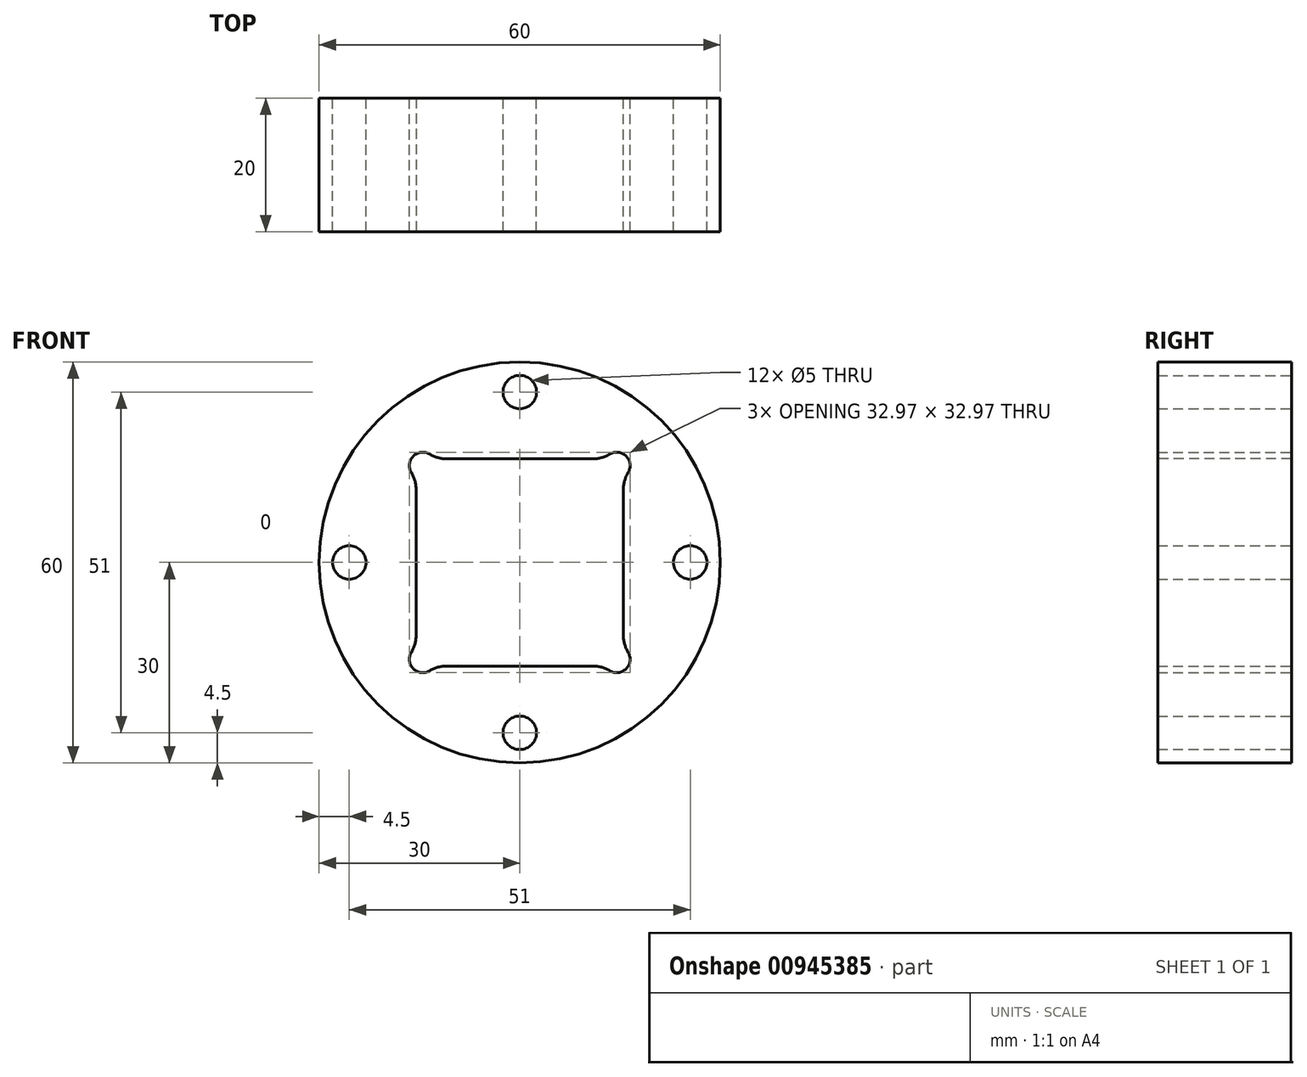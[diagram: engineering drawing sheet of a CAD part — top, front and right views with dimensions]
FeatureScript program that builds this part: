
annotation { "Feature Type Name" : "Feature", "Feature Type Description" : "" }
export const myFeature = defineFeature(function(context is Context, id is Id, definition is map)
    precondition{}
    {
        {
            var Q0;
            Q0=qCreatedBy(makeId("Front.planeOp"),FACE);
            var sketch = newSketch(context, id + "F0", { "sketchPlane" : qUnion([Q0])});
            skCircle(sketch, "E0", {"center": v(0, 0) * mm, "radius": 30 * mm});
            skCircle(sketch, "E1", {"center": v(0, 25.5) * mm, "radius": 2.5 * mm});
            skLineSegment(sketch, "E2", {"start": v(0, 0) * mm, "end": v(-35.32, 35.32) * mm, "construction": true});
            skCircle(sketch, "E3.MirrorC", {"center": v(-25.5, 0) * mm, "radius": 2.5 * mm});
            skCircle(sketch, "E4.MirrorC", {"center": v(0, -25.5) * mm, "radius": 2.5 * mm});
            skCircle(sketch, "E5.MirrorC", {"center": v(25.5, 0) * mm, "radius": 2.5 * mm});
            skSolve(sketch);
        }
        {
            var Q0;
            Q0=makeQuery(id+"F0.imprint","IMPRINT",FACE,{"disambiguationData":[TD([[makeQuery(id+"F0.imprint","IMPRINT",EDGE,{"derivedFrom":sQuery(id+"F0.wireOp",EDGE,"E0")}),1.0]])]});
            extrude(context, id + "F1", {"entities" : qUnion([Q0]), "depth" : 20 * mm, "offsetDistance" : 25 * mm});
        }
        {
            var Q0;
            Q0=qCreatedBy(makeId("Front.planeOp"),FACE);
            var sketch = newSketch(context, id + "F2", { "sketchPlane" : qUnion([Q0])});
            skLineSegment(sketch, "E6.bottom", {"start": v(-15.5, -15.5) * mm, "end": v(15.5, -15.5) * mm});
            skLineSegment(sketch, "E6.top", {"start": v(-15.5, 15.5) * mm, "end": v(15.5, 15.5) * mm});
            skLineSegment(sketch, "E6.left", {"start": v(-15.5, -15.5) * mm, "end": v(-15.5, 15.5) * mm});
            skLineSegment(sketch, "E6.right", {"start": v(15.5, -15.5) * mm, "end": v(15.5, 15.5) * mm});
            skPoint(sketch, "E6.middle", {"position": v(0, 0) * mm});
            skSolve(sketch);
        }
        {
            var Q0;
            Q0 = qSketchRegion(id + "F2", true);
            extrude(context, id + "F3", {"entities" : qUnion([Q0]), "operationType" : NewBodyOperationType.REMOVE, "endBound" : BoundingType.THROUGH_ALL, "depth" : 25 * mm, "offsetDistance" : 25 * mm});
        }
        {
            var Q0;
            Q0=qCreatedBy(makeId("Front.planeOp"),FACE);
            var sketch = newSketch(context, id + "F4", { "sketchPlane" : qUnion([Q0])});
            skCircle(sketch, "E7", {"center": v(-14.5, 14.5) * mm, "radius": 2 * mm});
            skCircle(sketch, "E8.MirrorC", {"center": v(14.5, 14.5) * mm, "radius": 2 * mm});
            skCircle(sketch, "E9.MirrorC", {"center": v(14.5, -14.5) * mm, "radius": 2 * mm});
            skCircle(sketch, "E10.MirrorC", {"center": v(-14.5, -14.5) * mm, "radius": 2 * mm});
            skSolve(sketch);
        }
        {
            var Q0;
            Q0 = qSketchRegion(id + "F4", true);
            extrude(context, id + "F5", {"entities" : qUnion([Q0]), "operationType" : NewBodyOperationType.REMOVE, "endBound" : BoundingType.THROUGH_ALL, "depth" : 25 * mm, "offsetDistance" : 25 * mm});
        }
        {
            var Q0;
            Q0=makeQuery(id+"F5.boolean.opBoolean","INTERSECT",EDGE,{"derivedFrom":[makeQuery(id+"F3.boolean.opBoolean","COPY",FACE,{"derivedFrom":makeQuery(id+"F3.opExtrude","SWEPT_FACE",FACE,{"disambiguationData":[OSD([sQuery(id+"F2.wireOp",EDGE,"E6.top")])]})}),makeQuery(id+"F5.opExtrude","SWEPT_FACE",FACE,{"disambiguationData":[OSD([sQuery(id+"F4.wireOp",EDGE,"E7")])]})]});
            var Q1;
            Q1=makeQuery(id+"F5.boolean.opBoolean","INTERSECT",EDGE,{"derivedFrom":[makeQuery(id+"F3.boolean.opBoolean","COPY",FACE,{"derivedFrom":makeQuery(id+"F3.opExtrude","SWEPT_FACE",FACE,{"disambiguationData":[OSD([sQuery(id+"F2.wireOp",EDGE,"E6.left")])]})}),makeQuery(id+"F5.opExtrude","SWEPT_FACE",FACE,{"disambiguationData":[OSD([sQuery(id+"F4.wireOp",EDGE,"E7")])]})]});
            var Q2;
            Q2=makeQuery(id+"F5.boolean.opBoolean","INTERSECT",EDGE,{"derivedFrom":[makeQuery(id+"F3.boolean.opBoolean","COPY",FACE,{"derivedFrom":makeQuery(id+"F3.opExtrude","SWEPT_FACE",FACE,{"disambiguationData":[OSD([sQuery(id+"F2.wireOp",EDGE,"E6.left")])]})}),makeQuery(id+"F5.opExtrude","SWEPT_FACE",FACE,{"disambiguationData":[OSD([sQuery(id+"F4.wireOp",EDGE,"E10.MirrorC")])]})]});
            var Q3;
            Q3=makeQuery(id+"F5.boolean.opBoolean","INTERSECT",EDGE,{"derivedFrom":[makeQuery(id+"F3.boolean.opBoolean","COPY",FACE,{"derivedFrom":makeQuery(id+"F3.opExtrude","SWEPT_FACE",FACE,{"disambiguationData":[OSD([sQuery(id+"F2.wireOp",EDGE,"E6.bottom")])]})}),makeQuery(id+"F5.opExtrude","SWEPT_FACE",FACE,{"disambiguationData":[OSD([sQuery(id+"F4.wireOp",EDGE,"E10.MirrorC")])]})]});
            var Q4;
            Q4=makeQuery(id+"F5.boolean.opBoolean","INTERSECT",EDGE,{"derivedFrom":[makeQuery(id+"F3.boolean.opBoolean","COPY",FACE,{"derivedFrom":makeQuery(id+"F3.opExtrude","SWEPT_FACE",FACE,{"disambiguationData":[OSD([sQuery(id+"F2.wireOp",EDGE,"E6.bottom")])]})}),makeQuery(id+"F5.opExtrude","SWEPT_FACE",FACE,{"disambiguationData":[OSD([sQuery(id+"F4.wireOp",EDGE,"E9.MirrorC")])]})]});
            var Q5;
            Q5=makeQuery(id+"F5.boolean.opBoolean","INTERSECT",EDGE,{"derivedFrom":[makeQuery(id+"F3.boolean.opBoolean","COPY",FACE,{"derivedFrom":makeQuery(id+"F3.opExtrude","SWEPT_FACE",FACE,{"disambiguationData":[OSD([sQuery(id+"F2.wireOp",EDGE,"E6.right")])]})}),makeQuery(id+"F5.opExtrude","SWEPT_FACE",FACE,{"disambiguationData":[OSD([sQuery(id+"F4.wireOp",EDGE,"E9.MirrorC")])]})]});
            var Q6;
            Q6=makeQuery(id+"F5.boolean.opBoolean","INTERSECT",EDGE,{"derivedFrom":[makeQuery(id+"F3.boolean.opBoolean","COPY",FACE,{"derivedFrom":makeQuery(id+"F3.opExtrude","SWEPT_FACE",FACE,{"disambiguationData":[OSD([sQuery(id+"F2.wireOp",EDGE,"E6.right")])]})}),makeQuery(id+"F5.opExtrude","SWEPT_FACE",FACE,{"disambiguationData":[OSD([sQuery(id+"F4.wireOp",EDGE,"E8.MirrorC")])]})]});
            var Q7;
            Q7=makeQuery(id+"F5.boolean.opBoolean","INTERSECT",EDGE,{"derivedFrom":[makeQuery(id+"F3.boolean.opBoolean","COPY",FACE,{"derivedFrom":makeQuery(id+"F3.opExtrude","SWEPT_FACE",FACE,{"disambiguationData":[OSD([sQuery(id+"F2.wireOp",EDGE,"E6.top")])]})}),makeQuery(id+"F5.opExtrude","SWEPT_FACE",FACE,{"disambiguationData":[OSD([sQuery(id+"F4.wireOp",EDGE,"E8.MirrorC")])]})]});
            fillet(context, id + "F6", {"entities" : qUnion([Q0, Q1, Q2, Q3, Q4, Q5, Q6, Q7]), "radius" : 5 * mm, "tangentPropagation" : true, "allowEdgeOverflow" : false});
        }
    });
